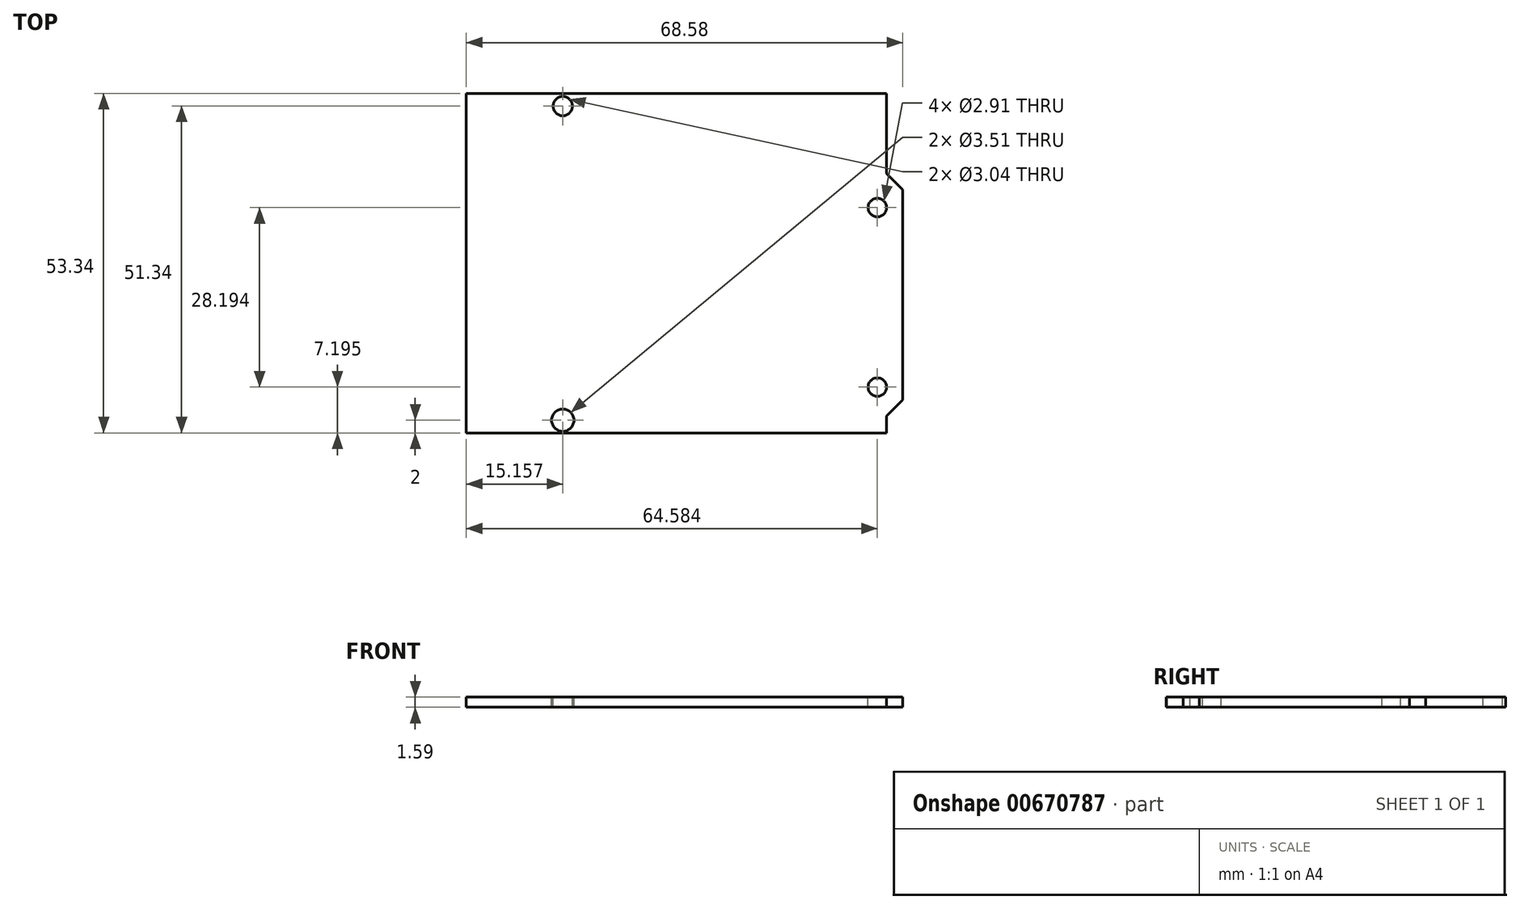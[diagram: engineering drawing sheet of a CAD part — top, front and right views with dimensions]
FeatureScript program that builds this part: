
annotation { "Feature Type Name" : "Feature", "Feature Type Description" : "" }
export const myFeature = defineFeature(function(context is Context, id is Id, definition is map)
    precondition{}
    {
        {
            var Q0;
            Q0=qCreatedBy(makeId("Top.planeOp"),FACE);
            var sketch = newSketch(context, id + "F0", { "sketchPlane" : qUnion([Q0])});
            skLineSegment(sketch, "E0", {"start": v(-33.02, 26.67) * mm, "end": v(-33.02, -26.67) * mm});
            skLineSegment(sketch, "E1", {"start": v(-33.02, -26.67) * mm, "end": v(33.02, -26.67) * mm});
            skLineSegment(sketch, "E2", {"start": v(33.02, -26.67) * mm, "end": v(33.02, 26.67) * mm});
            skLineSegment(sketch, "E3", {"start": v(33.02, 26.67) * mm, "end": v(-33.02, 26.67) * mm});
            skLineSegment(sketch, "E4", {"start": v(0, 26.67) * mm, "end": v(0, 0) * mm, "construction": true});
            skLineSegment(sketch, "E5", {"start": v(0, 0) * mm, "end": v(-33.02, 0) * mm, "construction": true});
            skLineSegment(sketch, "E6", {"start": v(33.02, -24) * mm, "end": v(35.56, -21.46) * mm});
            skLineSegment(sketch, "E7", {"start": v(35.56, -21.46) * mm, "end": v(35.56, 11.56) * mm});
            skLineSegment(sketch, "E8", {"start": v(35.56, 11.56) * mm, "end": v(33.02, 14.1) * mm});
            skSolve(sketch);
        }
        {
            var Q0;
            Q0 = qSketchRegion(id + "F0", true);
            extrude(context, id + "F1", {"entities" : qUnion([Q0]), "depth" : 1.59 * mm, "offsetDistance" : 25 * mm});
        }
        {
            var Q0;
            Q0=makeQuery(id+"F1.opExtrude","CAP_FACE",FACE,{"disambiguationData":[OSD([sQuery(id+"F0.wireOp",EDGE,"E0"),sQuery(id+"F0.wireOp",EDGE,"E1"),sQuery(id+"F0.wireOp",EDGE,"E2"),sQuery(id+"F0.wireOp",EDGE,"E3"),sQuery(id+"F0.wireOp",EDGE,"E6"),sQuery(id+"F0.wireOp",EDGE,"E7"),sQuery(id+"F0.wireOp",EDGE,"E8")])],"isStart":false});
            var sketch = newSketch(context, id + "F2", { "sketchPlane" : qUnion([Q0])});
            skCircle(sketch, "E9", {"center": v(-17.86, 24.67) * mm, "radius": 1.52 * mm});
            skCircle(sketch, "E10", {"center": v(-17.86, -24.67) * mm, "radius": 1.76 * mm});
            skCircle(sketch, "E11", {"center": v(31.56, -19.48) * mm, "radius": 1.46 * mm});
            skCircle(sketch, "E12", {"center": v(31.56, 8.72) * mm, "radius": 1.46 * mm});
            skSolve(sketch);
        }
        {
            var Q0;
            Q0 = qSketchRegion(id + "F2", true);
            extrude(context, id + "F3", {"entities" : qUnion([Q0]), "operationType" : NewBodyOperationType.REMOVE, "oppositeDirection" : true, "depth" : 25 * mm, "offsetDistance" : 25 * mm});
        }
    });
